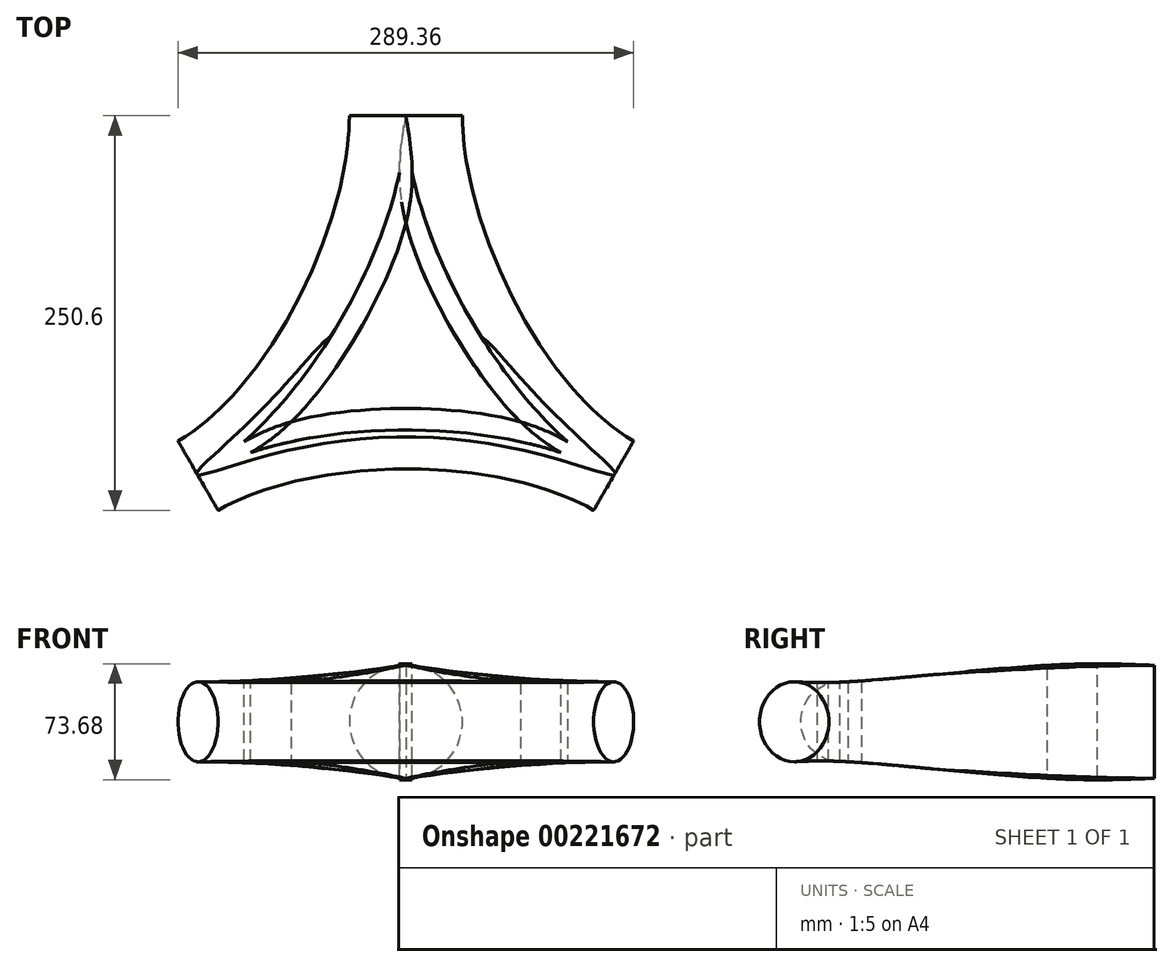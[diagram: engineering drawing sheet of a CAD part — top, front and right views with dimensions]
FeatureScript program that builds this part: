
annotation { "Feature Type Name" : "Feature", "Feature Type Description" : "" }
export const myFeature = defineFeature(function(context is Context, id is Id, definition is map)
    precondition{}
    {
        {
            var Q0;
            Q0=qCreatedBy(makeId("Top.planeOp"),FACE);
            var sketch = newSketch(context, id + "F0", { "sketchPlane" : qUnion([Q0])});
            skLineSegment(sketch, "E0", {"start": v(0, 0) * mm, "end": v(0, 152.4) * mm});
            skLineSegment(sketch, "E1", {"start": v(0, 0) * mm, "end": v(-131.98, -76.2) * mm});
            skLineSegment(sketch, "E2", {"start": v(0, 0) * mm, "end": v(131.98, -76.2) * mm});
            skSolve(sketch);
        }
        {
            var Q0;
            Q0=sQuery(id+"F0.wireOp",VERTEX,"E0.end");
            var Q1;
            Q1=sQuery(id+"F0.wireOp",EDGE,"E0");
            cPlane(context, id + "F1", {"entities" : qUnion([Q0, Q1]), "cplaneType" : CPlaneType.LINE_POINT, "offset" : 25.4 * mm, "width" : 152.4 * mm, "height" : 152.4 * mm});
        }
        {
            var Q0;
            Q0=sQuery(id+"F0.wireOp",VERTEX,"E1.end");
            var Q1;
            Q1=sQuery(id+"F0.wireOp",EDGE,"E1");
            cPlane(context, id + "F2", {"entities" : qUnion([Q0, Q1]), "cplaneType" : CPlaneType.LINE_POINT, "offset" : 25.4 * mm, "width" : 152.4 * mm, "height" : 152.4 * mm});
        }
        {
            var Q0;
            Q0=qCreatedBy(id+"F1.planeOp",FACE);
            var sketch = newSketch(context, id + "F3", { "sketchPlane" : qUnion([Q0])});
            skArc(sketch, "E3", {"start": v(0, -35.92) * mm, "mid": v(35.92, 0) * mm, "end": v(0, 35.92) * mm});
            skLineSegment(sketch, "E4", {"start": v(0, 35.92) * mm, "end": v(0, -35.92) * mm});
            skSolve(sketch);
        }
        {
            var Q0;
            Q0=qCreatedBy(id+"F2.planeOp",FACE);
            var sketch = newSketch(context, id + "F4", { "sketchPlane" : qUnion([Q0])});
            skArc(sketch, "E5", {"start": v(0, 25.4) * mm, "mid": v(-25.4, 0) * mm, "end": v(0, -25.4) * mm});
            skLineSegment(sketch, "E6", {"start": v(0, -25.4) * mm, "end": v(0, 25.4) * mm});
            skSolve(sketch);
        }
        {
            var Q0;
            Q0=qCreatedBy(makeId("Top.planeOp"),FACE);
            var sketch = newSketch(context, id + "F5", { "sketchPlane" : qUnion([Q0])});
            skLineSegment(sketch, "E7", {"start": v(-35.92, 166.9) * mm, "end": v(-35.92, 152.4) * mm});
            skLineSegment(sketch, "E8", {"start": v(-144.68, -54.2) * mm, "end": v(-194.22, -82.8) * mm});
            skFitSpline(sketch, "E9", {"points": [v(-35.92, 152.4) * mm, v(-144.68, -54.2) * mm], "startDerivative": vector(0, -228.6) * mm, "endDerivative": vector(-197.97, -114.3) * mm});
            skSolve(sketch);
        }
        {
            var Q0;
            Q0=qCreatedBy(makeId("Top.planeOp"),FACE);
            var sketch = newSketch(context, id + "F6", { "sketchPlane" : qUnion([Q0])});
            skFitSpline(sketch, "E10", {"points": [v(0, 152.4) * mm, v(-131.98, -76.2) * mm], "startDerivative": vector(0, -247.18) * mm, "endDerivative": vector(-157.44, -90.9) * mm});
            skFitSpline(sketch, "E11", {"points": [v(0, 152.4) * mm, v(131.98, -76.2) * mm], "startDerivative": vector(0, -247.18) * mm, "endDerivative": vector(154.97, -89.47) * mm});
            skFitSpline(sketch, "E12", {"points": [v(-131.98, -76.2) * mm, v(131.98, -76.2) * mm], "startDerivative": vector(157.44, 90.9) * mm, "endDerivative": vector(154.97, -89.47) * mm});
            skSolve(sketch);
        }
        {
            var Q0;
            Q0=makeQuery(id+"F3.imprint","IMPRINT",FACE,{"disambiguationData":[TD([[makeQuery(id+"F3.imprint","IMPRINT",EDGE,{"derivedFrom":sQuery(id+"F3.wireOp",EDGE,"E3")}),1.0]])]});
            var Q1;
            Q1=makeQuery(id+"F4.imprint","IMPRINT",FACE,{"disambiguationData":[TD([[makeQuery(id+"F4.imprint","IMPRINT",EDGE,{"derivedFrom":sQuery(id+"F4.wireOp",EDGE,"E5")}),1.0]])]});
            var Q2;
            Q2=makeQuery(id+"FoTPBo07PUCdWoR_1.boolean.opBoolean","INTERSECT",EDGE,{"derivedFrom":[makeQuery(id+"Fmqj505uHOoOAdz_0.opExtrude","SWEPT_FACE",FACE,{"disambiguationData":[OSD([sQuery(id+"F6.wireOp",EDGE,"E10")])]}),makeQuery(id+"FoTPBo07PUCdWoR_1.opExtrude","SWEPT_FACE",FACE,{"disambiguationData":[OSD([sQuery(id+"F1sg6nbBEsbhiTy_1.wireOp",EDGE,"7777b7bf-7085-4bd1-be5a-26a7b610b709")])]})]});
            loft(context, id + "F7", {"startCondition" : LoftEndDerivativeType.NORMAL_TO_PROFILE, "startMagnitude" : 1, "endCondition" : LoftEndDerivativeType.NORMAL_TO_PROFILE, "endMagnitude" : 1, "sheetProfilesArray" : [{ "sheetProfileEntities" : qUnion([Q0]) }, { "sheetProfileEntities" : qUnion([Q1]) }], "guidesArray" : [{ "guideEntities" : qUnion([Q2]), "guideDerivativeType" : LoftGuideDerivativeType.DEFAULT, "guideDerivativeMagnitude" : 1 }]});
        }
        {
            var Q0;
            Q0=makeQuery(id+"F7.opLoft","SWEPT_BODY",BODY,{"disambiguationData":[OSD([makeQuery(id+"F3.imprint","IMPRINT",FACE,{"disambiguationData":[TD([[makeQuery(id+"F3.imprint","IMPRINT",EDGE,{"derivedFrom":sQuery(id+"F3.wireOp",EDGE,"E3")}),1.0]])]}),makeQuery(id+"F4.imprint","IMPRINT",FACE,{"disambiguationData":[TD([[makeQuery(id+"F4.imprint","IMPRINT",EDGE,{"derivedFrom":sQuery(id+"F4.wireOp",EDGE,"E5")}),1.0]])]})])]});
            var Q1;
            Q1=qCreatedBy(makeId("Right.planeOp"),FACE);
            mirror(context, id + "F8", {"entities" : qUnion([Q0]), "mirrorPlane" : qUnion([Q1])});
        }
        {
            var Q0;
            Q0=makeQuery(id+"F8.opPattern","COPY",FACE,{"derivedFrom":makeQuery(id+"F7.opLoft","CAP_FACE",FACE,{"disambiguationData":[OSD([makeQuery(id+"F4.imprint","IMPRINT",FACE,{"disambiguationData":[TD([[makeQuery(id+"F4.imprint","IMPRINT",EDGE,{"derivedFrom":sQuery(id+"F4.wireOp",EDGE,"E5")}),1.0]])]})])],"isStart":true}),"instanceName":"1"});
            var sketch = newSketch(context, id + "F9", { "sketchPlane" : qUnion([Q0])});
            skArc(sketch, "E13", {"start": v(0, 25.4) * mm, "mid": v(-25.4, 0) * mm, "end": v(0, -25.4) * mm});
            skLineSegment(sketch, "E14", {"start": v(0, 25.4) * mm, "end": v(0, -25.4) * mm});
            skSolve(sketch);
        }
        {
            var Q0;
            Q0=makeQuery(id+"F7.opLoft","CAP_FACE",FACE,{"disambiguationData":[OSD([makeQuery(id+"F4.imprint","IMPRINT",FACE,{"disambiguationData":[TD([[makeQuery(id+"F4.imprint","IMPRINT",EDGE,{"derivedFrom":sQuery(id+"F4.wireOp",EDGE,"E5")}),1.0]])]})])],"isStart":true});
            var sketch = newSketch(context, id + "F10", { "sketchPlane" : qUnion([Q0])});
            skArc(sketch, "E15", {"start": v(0, -25.4) * mm, "mid": v(25.4, 0) * mm, "end": v(0, 25.4) * mm});
            skLineSegment(sketch, "E16", {"start": v(0, 25.4) * mm, "end": v(0, -25.4) * mm});
            skSolve(sketch);
        }
        {
            var Q0;
            Q0=makeQuery(id+"F10.imprint","IMPRINT",FACE,{"disambiguationData":[TD([[makeQuery(id+"F10.imprint","IMPRINT",EDGE,{"derivedFrom":sQuery(id+"F10.wireOp",EDGE,"E15")}),1.0]])]});
            var Q1;
            Q1=makeQuery(id+"F9.imprint","IMPRINT",FACE,{"disambiguationData":[TD([[makeQuery(id+"F9.imprint","IMPRINT",EDGE,{"derivedFrom":sQuery(id+"F9.wireOp",EDGE,"E13")}),1.0]])]});
            loft(context, id + "F11", {"startCondition" : LoftEndDerivativeType.NORMAL_TO_PROFILE, "startMagnitude" : 1, "endCondition" : LoftEndDerivativeType.NORMAL_TO_PROFILE, "endMagnitude" : 1, "sheetProfilesArray" : [{ "sheetProfileEntities" : qUnion([Q0]) }, { "sheetProfileEntities" : qUnion([Q1]) }]});
        }
        {
            var Q0;
            Q0=qCreatedBy(makeId("Top.planeOp"),FACE);
            var sketch = newSketch(context, id + "F12", { "sketchPlane" : qUnion([Q0])});
            skFitSpline(sketch, "E17.0", {"points": [v(0, 152.4) * mm, v(0, 84.25) * mm, v(-72.96, -42.12) * mm, v(-131.98, -76.2) * mm]});
            skFitSpline(sketch, "E17.1", {"points": [v(0, 152.4) * mm, v(0, 84.25) * mm, v(72.96, -42.12) * mm, v(131.98, -76.2) * mm]});
            skFitSpline(sketch, "E17.2", {"points": [v(-131.98, -76.2) * mm, v(-72.93, -42.1) * mm, v(72.93, -42.1) * mm, v(131.98, -76.2) * mm]});
            skSolve(sketch);
        }
        {
            var Q0;
            Q0 = qSketchRegion(id + "F12", true);
            extrude(context, id + "F13", {"entities" : qUnion([Q0]), "operationType" : NewBodyOperationType.ADD, "endBound" : BoundingType.SYMMETRIC, "depth" : 158.5 * mm});
        }
        {
            var Q0;
            Q0=qCreatedBy(makeId("Right.planeOp"),FACE);
            var sketch = newSketch(context, id + "F14", { "sketchPlane" : qUnion([Q0])});
            skFitSpline(sketch, "E18.0", {"points": [v(152.4, -35.92) * mm, v(84.25, -35.92) * mm, v(-42.12, -25.4) * mm, v(-76.2, -25.4) * mm]});
            skLineSegment(sketch, "E19", {"start": v(152.4, -35.92) * mm, "end": v(152.4, -96.07) * mm});
            skLineSegment(sketch, "E20", {"start": v(152.4, -96.07) * mm, "end": v(-76.2, -96.07) * mm});
            skLineSegment(sketch, "E21", {"start": v(-76.2, -96.07) * mm, "end": v(-76.2, -25.4) * mm});
            skLineSegment(sketch, "E22.MirrorCS", {"start": v(152.4, 35.92) * mm, "end": v(152.4, 96.07) * mm});
            skFitSpline(sketch, "E23.MirrorCS", {"points": [v(152.4, 35.92) * mm, v(84.25, 35.92) * mm, v(-42.12, 25.4) * mm, v(-76.2, 25.4) * mm]});
            skLineSegment(sketch, "E24.MirrorCS", {"start": v(152.4, 96.07) * mm, "end": v(-76.2, 96.07) * mm});
            skLineSegment(sketch, "E25.MirrorCS", {"start": v(-76.2, 96.07) * mm, "end": v(-76.2, 25.4) * mm});
            skSolve(sketch);
        }
        {
            var Q0;
            Q0 = qSketchRegion(id + "F14", true);
            extrude(context, id + "F15", {"entities" : qUnion([Q0]), "operationType" : NewBodyOperationType.REMOVE, "endBound" : BoundingType.SYMMETRIC, "oppositeDirection" : true, "depth" : 352.04 * mm});
        }
    });
